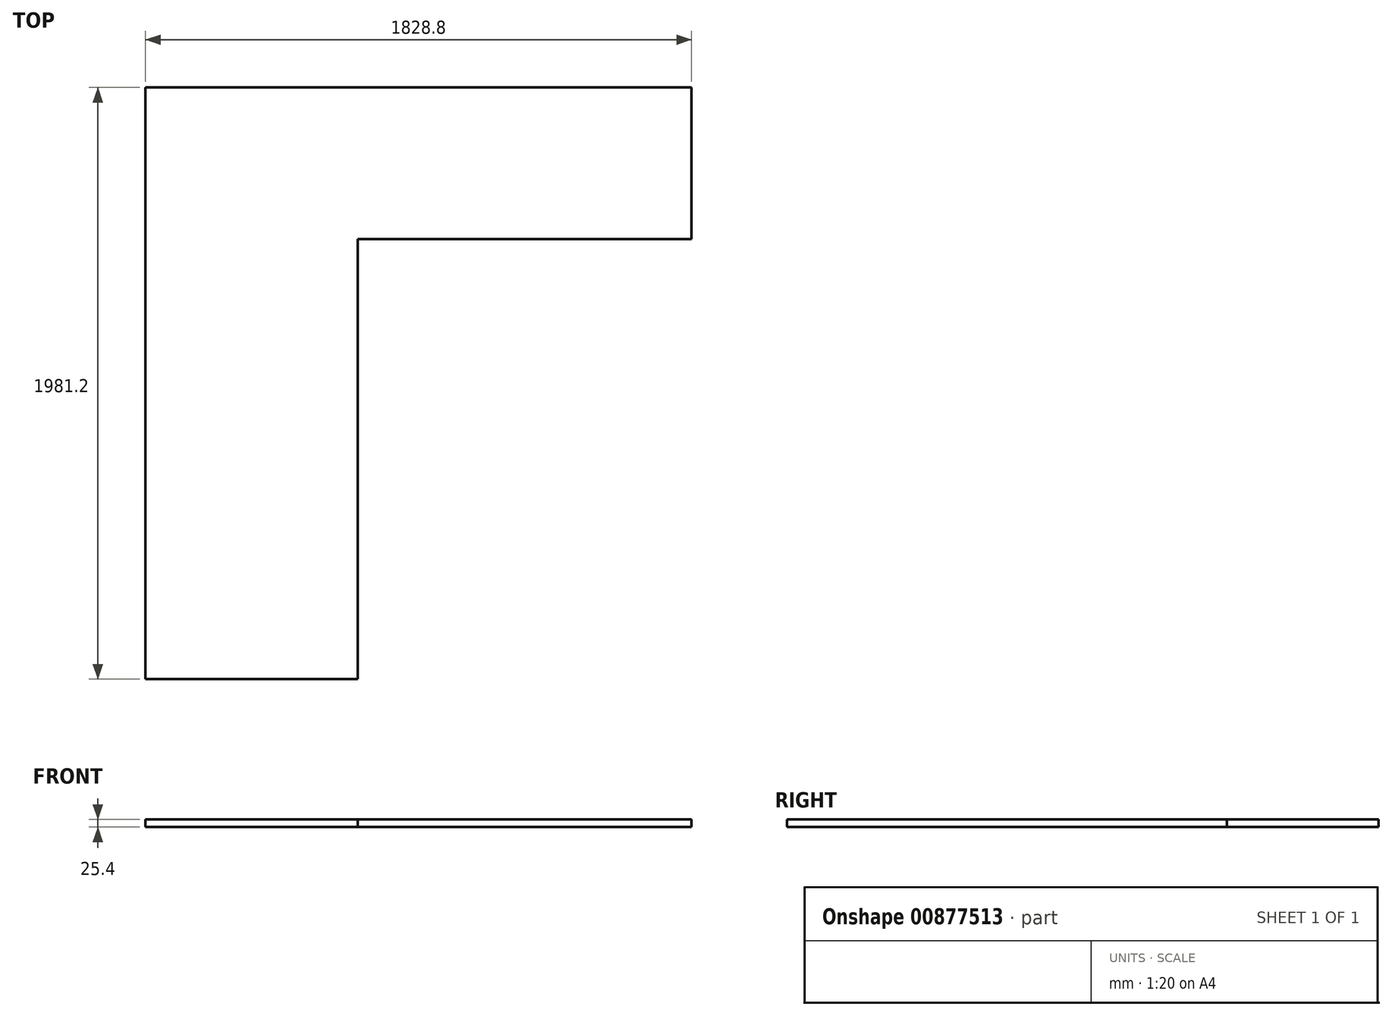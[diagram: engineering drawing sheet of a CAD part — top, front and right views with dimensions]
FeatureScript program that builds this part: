
annotation { "Feature Type Name" : "Feature", "Feature Type Description" : "" }
export const myFeature = defineFeature(function(context is Context, id is Id, definition is map)
    precondition{}
    {
        {
            var Q0;
            Q0=qCreatedBy(makeId("Top.planeOp"),FACE);
            var sketch = newSketch(context, id + "F0", { "sketchPlane" : qUnion([Q0])});
            skLineSegment(sketch, "E0", {"start": v(0, 0) * mm, "end": v(1117.6, 0) * mm});
            skLineSegment(sketch, "E1", {"start": v(1117.6, 0) * mm, "end": v(1117.6, 508) * mm});
            skLineSegment(sketch, "E2", {"start": v(1117.6, 508) * mm, "end": v(-711.2, 508) * mm});
            skLineSegment(sketch, "E3", {"start": v(-711.2, 508) * mm, "end": v(-711.2, -1473.2) * mm});
            skLineSegment(sketch, "E4", {"start": v(-711.2, -1473.2) * mm, "end": v(0, -1473.2) * mm});
            skLineSegment(sketch, "E5", {"start": v(0, -1473.2) * mm, "end": v(0, 0) * mm});
            skSolve(sketch);
        }
        {
            var Q0;
            Q0=makeQuery(id+"F0.imprint","IMPRINT",FACE,{"disambiguationData":[TD([[makeQuery(id+"F0.imprint","IMPRINT",EDGE,{"derivedFrom":sQuery(id+"F0.wireOp",EDGE,"E0")}),1.0]])]});
            extrude(context, id + "F1", {"entities" : qUnion([Q0]), "depth" : 25.4 * mm, "offsetDistance" : 25.4 * mm});
        }
    });
